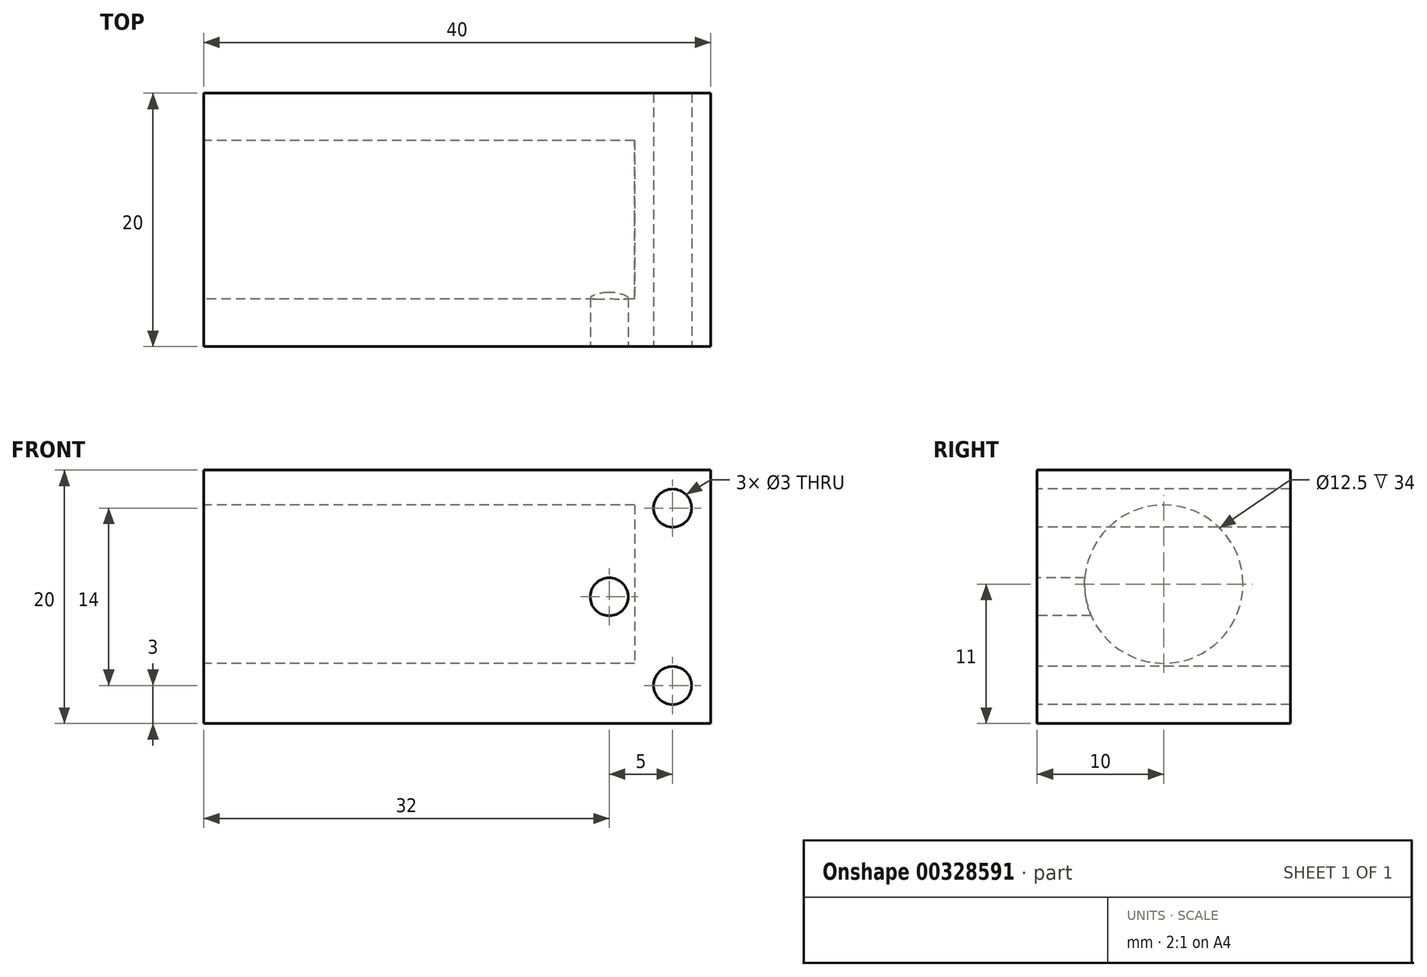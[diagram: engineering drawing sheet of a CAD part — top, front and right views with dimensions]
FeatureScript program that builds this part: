
annotation { "Feature Type Name" : "Feature", "Feature Type Description" : "" }
export const myFeature = defineFeature(function(context is Context, id is Id, definition is map)
    precondition{}
    {
        {
            var Q0;
            Q0=qCreatedBy(makeId("Front.planeOp"),FACE);
            var sketch = newSketch(context, id + "F0", { "sketchPlane" : qUnion([Q0])});
            skLineSegment(sketch, "E0.bottom", {"start": v(20, 10) * mm, "end": v(-20, 10) * mm});
            skLineSegment(sketch, "E0.top", {"start": v(20, -10) * mm, "end": v(-20, -10) * mm});
            skLineSegment(sketch, "E0.left", {"start": v(20, 10) * mm, "end": v(20, -10) * mm});
            skLineSegment(sketch, "E0.right", {"start": v(-20, 10) * mm, "end": v(-20, -10) * mm});
            skPoint(sketch, "E0.middle", {"position": v(0, 0) * mm});
            skSolve(sketch);
        }
        {
            var Q0;
            Q0 = qSketchRegion(id + "F0", true);
            extrude(context, id + "F1", {"entities" : qUnion([Q0]), "depth" : 10 * mm, "hasSecondDirection" : true, "secondDirectionOppositeDirection" : true, "secondDirectionDepth" : 10 * mm});
        }
        {
            var Q0;
            Q0=makeQuery(id+"F1.opExtrude","SWEPT_FACE",FACE,{"disambiguationData":[OSD([sQuery(id+"F0.wireOp",EDGE,"E0.right")])]});
            var sketch = newSketch(context, id + "F2", { "sketchPlane" : qUnion([Q0])});
            skCircle(sketch, "E1", {"center": v(0, 1) * mm, "radius": 6.25 * mm});
            skSolve(sketch);
        }
        {
            var Q0;
            Q0 = qSketchRegion(id + "F2", true);
            extrude(context, id + "F3", {"entities" : qUnion([Q0]), "operationType" : NewBodyOperationType.REMOVE, "oppositeDirection" : true, "depth" : 34 * mm});
        }
        {
            var Q0;
            Q0=makeQuery(id+"F1.opExtrude","CAP_FACE",FACE,{"disambiguationData":[OSD([sQuery(id+"F0.wireOp",EDGE,"E0.bottom"),sQuery(id+"F0.wireOp",EDGE,"E0.top"),sQuery(id+"F0.wireOp",EDGE,"E0.left"),sQuery(id+"F0.wireOp",EDGE,"E0.right")])],"isStart":false});
            var sketch = newSketch(context, id + "F4", { "sketchPlane" : qUnion([Q0])});
            skCircle(sketch, "E2", {"center": v(17, 7) * mm, "radius": 1.5 * mm});
            skCircle(sketch, "E3", {"center": v(17, -7) * mm, "radius": 1.5 * mm});
            skSolve(sketch);
        }
        {
            var Q0;
            Q0 = qSketchRegion(id + "F4", true);
            extrude(context, id + "F5", {"entities" : qUnion([Q0]), "operationType" : NewBodyOperationType.REMOVE, "endBound" : BoundingType.THROUGH_ALL, "oppositeDirection" : true, "depth" : 25 * mm});
        }
        {
            var Q0;
            Q0=makeQuery(id+"F1.opExtrude","CAP_FACE",FACE,{"disambiguationData":[OSD([sQuery(id+"F0.wireOp",EDGE,"E0.bottom"),sQuery(id+"F0.wireOp",EDGE,"E0.top"),sQuery(id+"F0.wireOp",EDGE,"E0.left"),sQuery(id+"F0.wireOp",EDGE,"E0.right")])],"isStart":false});
            var sketch = newSketch(context, id + "F6", { "sketchPlane" : qUnion([Q0])});
            skCircle(sketch, "E4", {"center": v(12, 0) * mm, "radius": 1.5 * mm});
            skSolve(sketch);
        }
        {
            var Q0;
            Q0 = qSketchRegion(id + "F6", true);
            extrude(context, id + "F7", {"entities" : qUnion([Q0]), "operationType" : NewBodyOperationType.REMOVE, "endBound" : BoundingType.UP_TO_NEXT, "oppositeDirection" : true, "depth" : 25 * mm});
        }
    });
